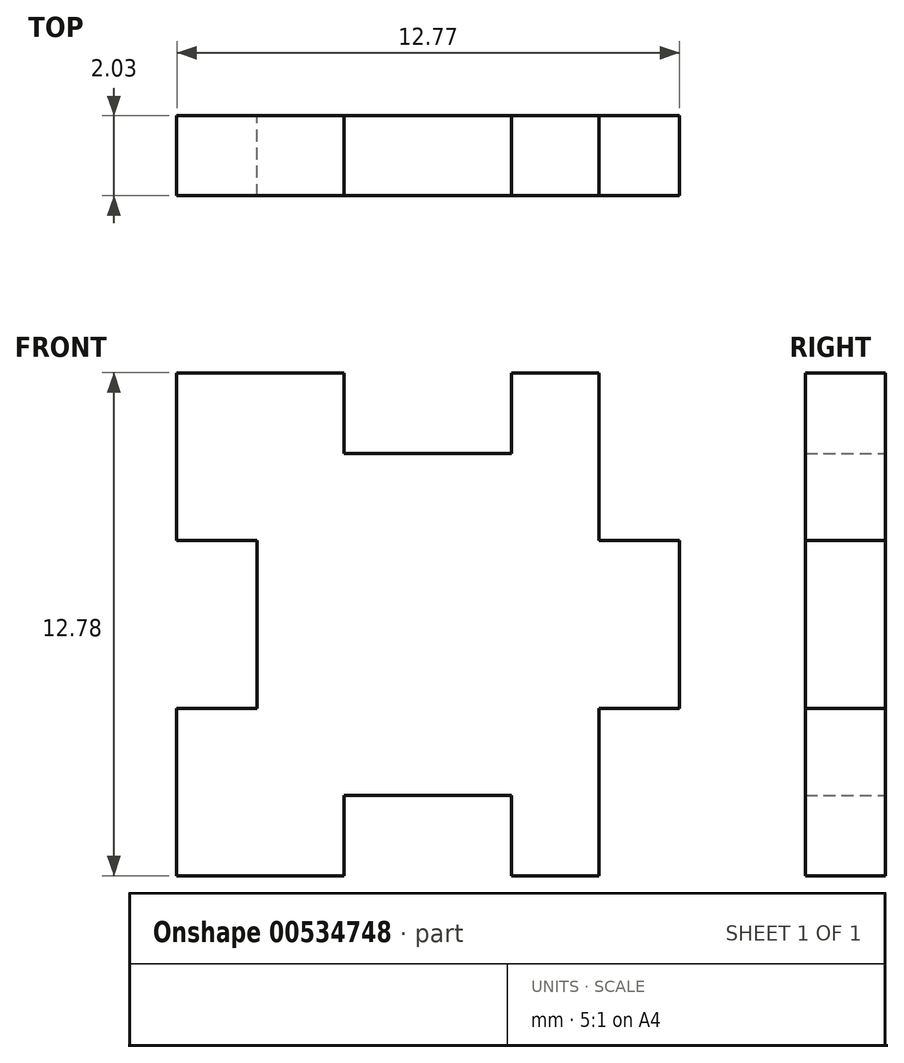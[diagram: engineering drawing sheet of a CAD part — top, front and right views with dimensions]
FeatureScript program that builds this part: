
annotation { "Feature Type Name" : "Feature", "Feature Type Description" : "" }
export const myFeature = defineFeature(function(context is Context, id is Id, definition is map)
    precondition{}
    {
        {
            var Q0;
            Q0=qCreatedBy(makeId("Front.planeOp"),FACE);
            var sketch = newSketch(context, id + "F0", { "sketchPlane" : qUnion([Q0])});
            skLineSegment(sketch, "E0", {"start": v(-10.99, 26.89) * mm, "end": v(-10.99, 29.02) * mm});
            skLineSegment(sketch, "E1", {"start": v(-10.99, 29.02) * mm, "end": v(-13.03, 29.02) * mm});
            skLineSegment(sketch, "E2", {"start": v(-13.03, 29.02) * mm, "end": v(-13.03, 33.28) * mm});
            skLineSegment(sketch, "E3", {"start": v(-13.03, 33.28) * mm, "end": v(-8.78, 33.28) * mm});
            skLineSegment(sketch, "E4", {"start": v(-8.78, 33.28) * mm, "end": v(-8.78, 31.23) * mm});
            skLineSegment(sketch, "E5", {"start": v(-8.78, 31.23) * mm, "end": v(-4.53, 31.23) * mm});
            skLineSegment(sketch, "E6", {"start": v(-4.53, 31.23) * mm, "end": v(-4.53, 33.28) * mm});
            skLineSegment(sketch, "E7", {"start": v(-4.53, 33.28) * mm, "end": v(-2.3, 33.28) * mm});
            skLineSegment(sketch, "E8", {"start": v(-2.3, 33.28) * mm, "end": v(-2.3, 29.02) * mm});
            skLineSegment(sketch, "E9", {"start": v(-2.3, 29.02) * mm, "end": v(-0.26, 29.02) * mm});
            skLineSegment(sketch, "E10", {"start": v(-10.99, 26.89) * mm, "end": v(8.72, 26.89) * mm, "construction": true});
            skLineSegment(sketch, "E11.MirrorCS", {"start": v(-2.3, 24.76) * mm, "end": v(-0.26, 24.76) * mm});
            skLineSegment(sketch, "E12.MirrorCS", {"start": v(-2.3, 20.5) * mm, "end": v(-2.3, 24.76) * mm});
            skLineSegment(sketch, "E13.MirrorCS", {"start": v(-4.53, 20.5) * mm, "end": v(-2.3, 20.5) * mm});
            skLineSegment(sketch, "E14.MirrorCS", {"start": v(-4.53, 22.55) * mm, "end": v(-4.53, 20.5) * mm});
            skLineSegment(sketch, "E15.MirrorCS", {"start": v(-8.78, 22.55) * mm, "end": v(-4.53, 22.55) * mm});
            skLineSegment(sketch, "E16.MirrorCS", {"start": v(-8.78, 20.5) * mm, "end": v(-8.78, 22.55) * mm});
            skLineSegment(sketch, "E17.MirrorCS", {"start": v(-13.03, 20.5) * mm, "end": v(-8.78, 20.5) * mm});
            skLineSegment(sketch, "E18.MirrorCS", {"start": v(-13.03, 24.76) * mm, "end": v(-13.03, 20.5) * mm});
            skLineSegment(sketch, "E19.MirrorCS", {"start": v(-10.99, 24.76) * mm, "end": v(-13.03, 24.76) * mm});
            skLineSegment(sketch, "E20.MirrorCS", {"start": v(-10.99, 26.89) * mm, "end": v(-10.99, 24.76) * mm});
            skLineSegment(sketch, "E21", {"start": v(-0.26, 29.02) * mm, "end": v(-0.26, 24.76) * mm});
            skSolve(sketch);
        }
        {
            var Q0;
            Q0=makeQuery(id+"F0.imprint","IMPRINT",FACE,{"disambiguationData":[TD([[makeQuery(id+"F0.imprint","IMPRINT",EDGE,{"derivedFrom":sQuery(id+"F0.wireOp",EDGE,"E0")}),-1.0]])]});
            extrude(context, id + "F1", {"entities" : qUnion([Q0]), "depth" : 2.03 * mm, "offsetDistance" : 25.4 * mm});
        }
        {
            var Q0;
            Q0=qCreatedBy(makeId("Front.planeOp"),FACE);
            cPlane(context, id + "F2", {"entities" : qUnion([Q0]), "cplaneType" : CPlaneType.OFFSET, "offset" : 4.06 * mm, "width" : 152.4 * mm, "height" : 152.4 * mm});
        }
        {
            var Q0;
            Q0=qCreatedBy(id+"F2.planeOp",FACE);
            var sketch = newSketch(context, id + "F3", { "sketchPlane" : qUnion([Q0])});
            skText(sketch, "E22", { "text": "L", "fontName": "OpenSans-Regular.ttf"});
            const initialGuessF3  = {"E22": [-0.00901, 0.02411, 1, 0, 0.006]};
            skSetInitialGuess(sketch, initialGuessF3);
            skSolve(sketch);
        }
        {
            var Q0;
            Q0 = qSketchRegion(id + "F3", true);
            extrude(context, id + "F4", {"entities" : qUnion([Q0]), "operationType" : NewBodyOperationType.REMOVE, "oppositeDirection" : true, "depth" : 0.5 * mm, "offsetDistance" : 25.4 * mm});
        }
    });
